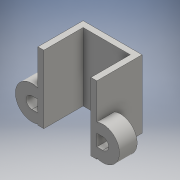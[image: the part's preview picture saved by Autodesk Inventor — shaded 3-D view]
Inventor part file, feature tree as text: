
AUTODESK INVENTOR PART (.ipt)
format: ipt  version: 2016 (Build 200138000, 138)  size: 144,384 bytes
history: native  units: mm
features: extrude x3, sketch x3, other x1
ambient origin geometry x8: Origin, YZ Plane, XZ Plane, XY Plane, X Axis, Y Axis, Z Axis, Center Point
bodies: Body1 (feature_tree)
feature tree (7):
  other  "Bryła1"
  extrude  "Wyciągnięcie proste1"  Depth=11.5mm TaperAngle=0.0deg
  extrude  "Wyciągnięcie proste2"  Depth=1.5mm
  extrude  "Wyciągnięcie proste3"  Depth=10.0mm
  sketch  "Szkic1"
  sketch  "Szkic2"
  sketch  "Szkic3"
